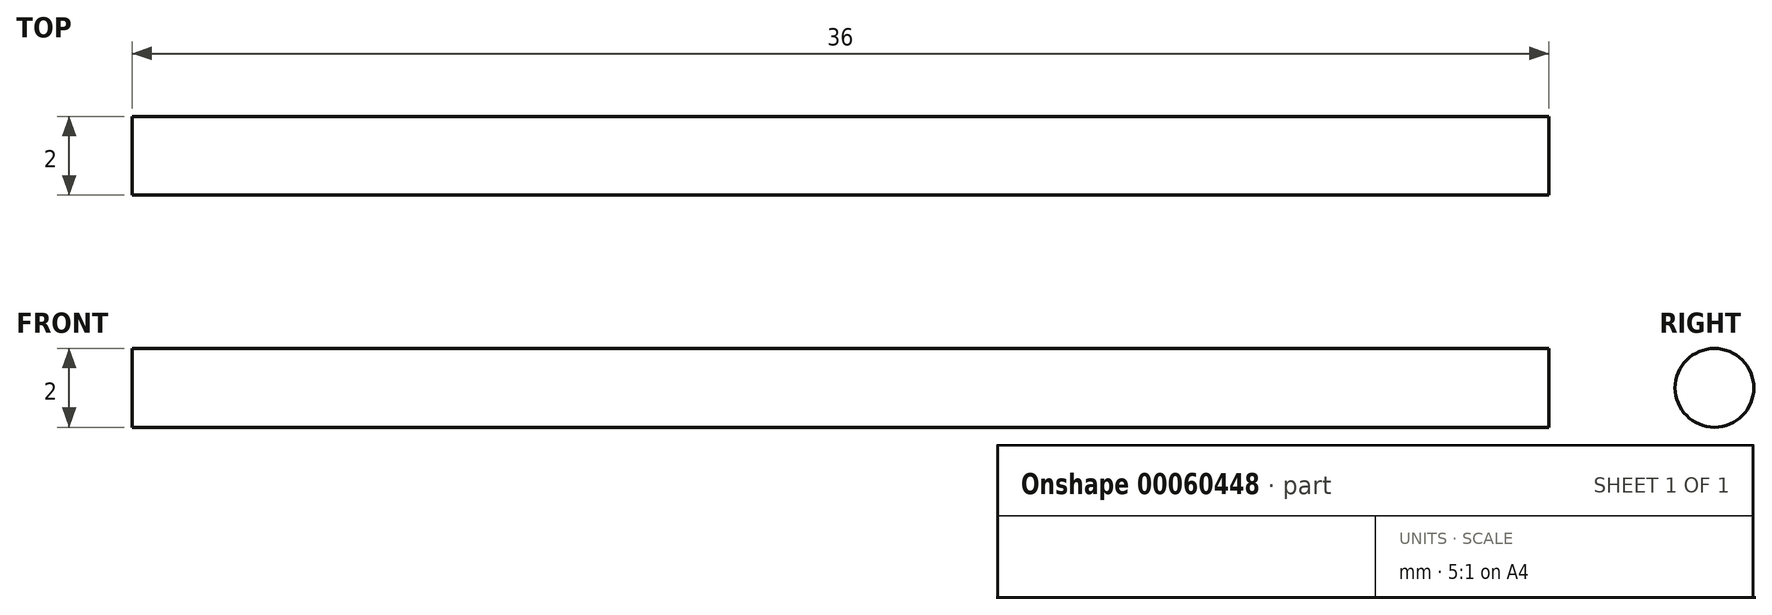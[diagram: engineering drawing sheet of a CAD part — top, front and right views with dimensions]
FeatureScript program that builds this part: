
annotation { "Feature Type Name" : "Feature", "Feature Type Description" : "" }
export const myFeature = defineFeature(function(context is Context, id is Id, definition is map)
    precondition{}
    {
        {
            var Q0;
            Q0=qCreatedBy(makeId("Right.planeOp"),FACE);
            var sketch = newSketch(context, id + "F0", { "sketchPlane" : qUnion([Q0])});
            skCircle(sketch, "E0", {"center": v(0, 0) * mm, "radius": 1 * mm});
            skSolve(sketch);
        }
        {
            var Q0;
            Q0 = qSketchRegion(id + "F0", true);
            extrude(context, id + "F1", {"entities" : qUnion([Q0]), "depth" : 36 * mm});
        }
    });
